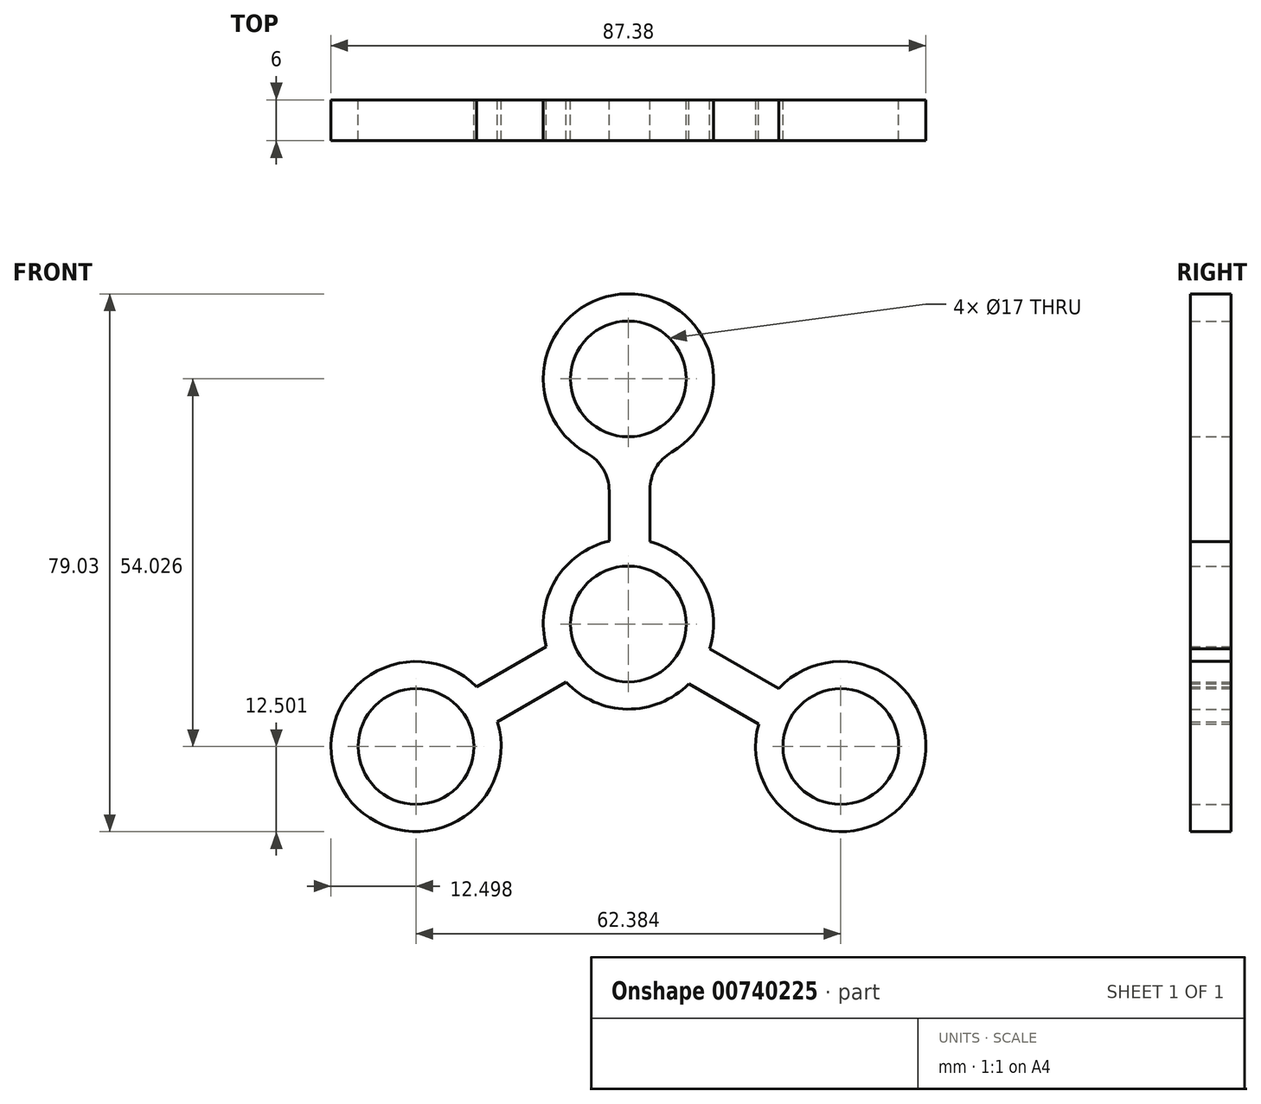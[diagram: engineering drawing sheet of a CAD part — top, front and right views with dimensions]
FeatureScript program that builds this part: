
annotation { "Feature Type Name" : "Feature", "Feature Type Description" : "" }
export const myFeature = defineFeature(function(context is Context, id is Id, definition is map)
    precondition{}
    {
        {
            var Q0;
            Q0=qCreatedBy(makeId("Front.planeOp"),FACE);
            var sketch = newSketch(context, id + "F0", { "sketchPlane" : qUnion([Q0])});
            skCircle(sketch, "E0", {"center": v(0, 0) * mm, "radius": 8.5 * mm});
            skCircle(sketch, "E1", {"center": v(0, 36.02) * mm, "radius": 8.5 * mm});
            skArc(sketch, "E2.0", {"start": v(6.31, 25.23) * mm, "mid": v(-0.13, 48.52) * mm, "end": v(-6.09, 25.1) * mm});
            skCircle(sketch, "E3.0", {"center": v(0, 0) * mm, "radius": 12.5 * mm});
            skLineSegment(sketch, "E4", {"start": v(-2.83, 19.55) * mm, "end": v(-2.83, 12.18) * mm});
            skLineSegment(sketch, "E5.0", {"start": v(3.17, 19.75) * mm, "end": v(3.17, 12.1) * mm});
            skArc(sketch, "E6.1.0", {"start": v(-22.3, -9.22) * mm, "mid": v(-41.93, -24.41) * mm, "end": v(-19.23, -14.37) * mm});
            skCircle(sketch, "E6.1.1", {"center": v(-31.2, -18) * mm, "radius": 8.5 * mm});
            skLineSegment(sketch, "E6.1.2", {"start": v(-22.59, -9.38) * mm, "end": v(-11.78, -3.14) * mm});
            skLineSegment(sketch, "E6.1.3", {"start": v(-19.23, -14.37) * mm, "end": v(-9.13, -8.54) * mm});
            skArc(sketch, "E6.2.0", {"start": v(19.13, -14.71) * mm, "mid": v(42.1, -24.1) * mm, "end": v(22.06, -9.47) * mm});
            skCircle(sketch, "E6.2.1", {"center": v(31.2, -18) * mm, "radius": 8.5 * mm});
            skLineSegment(sketch, "E6.2.2", {"start": v(19.42, -14.87) * mm, "end": v(8.6, -8.63) * mm});
            skLineSegment(sketch, "E6.2.3", {"start": v(22.06, -9.47) * mm, "end": v(11.96, -3.64) * mm});
            skPoint(sketch, "E7.orphan", {"position": v(3.17, 11.77) * mm});
            skPoint(sketch, "E8.orphan", {"position": v(3.17, 24.25) * mm});
            skPoint(sketch, "E9.visualSharp", {"position": v(3.17, 23.93) * mm});
            skArc(sketch, "E9.filletArc", {"start": v(6.31, 25.23) * mm, "mid": v(4.01, 22.9) * mm, "end": v(3.17, 19.75) * mm});
            skPoint(sketch, "E10.visualSharp", {"position": v(-2.83, 23.84) * mm});
            skArc(sketch, "E10.filletArc", {"start": v(-2.83, 19.55) * mm, "mid": v(-3.7, 22.77) * mm, "end": v(-6.09, 25.1) * mm});
            skSolve(sketch);
        }
        {
            var Q0;
            Q0=makeQuery(id+"F0.imprint","IMPRINT",FACE,{"disambiguationData":[TD([[makeQuery(id+"F0.imprint","IMPRINT",EDGE,{"derivedFrom":sQuery(id+"F0.wireOp",EDGE,"E0")}),-1.0]])]});
            var Q1;
            Q1=makeQuery(id+"F0.imprint","IMPRINT",FACE,{"disambiguationData":[TD([[makeQuery(id+"F0.imprint","IMPRINT",EDGE,{"derivedFrom":sQuery(id+"F0.wireOp",EDGE,"E1")}),-1.0]])]});
            var Q2;
            {var subQ1=sQuery(id+"F0.wireOp",EDGE,"E6.1.0");Q2=makeQuery(id+"F0.imprint","IMPRINT",FACE,{"disambiguationData":[TD([[makeQuery(id+"F0.imprint","IMPRINT",EDGE,{"derivedFrom":subQ1}),1.0]])]});}
            var Q3;
            {var subQ0=sQuery(id+"F0.wireOp",EDGE,"E6.2.0");Q3=makeQuery(id+"F0.imprint","IMPRINT",FACE,{"disambiguationData":[TD([[makeQuery(id+"F0.imprint","IMPRINT",EDGE,{"derivedFrom":subQ0}),1.0]])]});}
            extrude(context, id + "F1", {"entities" : qUnion([Q0, Q1, Q2, Q3]), "depth" : 6 * mm, "offsetDistance" : 25.4 * mm});
        }
    });
